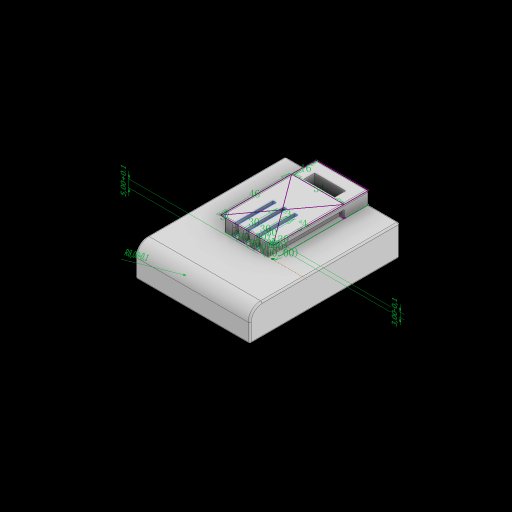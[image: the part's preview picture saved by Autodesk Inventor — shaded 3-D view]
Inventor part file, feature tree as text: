
AUTODESK INVENTOR PART (.ipt)
format: ipt  version: 2023 (Build 270158030, 158C)  size: 745,472 bytes
history: native  units: mm
features: extrude x9, sketch x7, fillet x7, other x3, chamfer x2
ambient origin geometry x8: Origin, YZ Plane, XZ Plane, XY Plane, X Axis, Y Axis, Z Axis, Center Point
bodies: 实体1 (feature_tree)
feature tree (28):
  extrude  "拉伸1"  Depth=46.0mm
  sketch  "草图2"  dims[d8=16.0mm d9=3.0mm]
  extrude  "拉伸2"  Depth=16.0mm
  extrude  "拉伸3"  Depth=5.0mm
  sketch  "草图4"  dims[d10=5.0mm d11=3.0mm]
  extrude  "拉伸4"  Depth=8.0mm TaperAngle=0.0deg
  extrude  "拉伸5"  Depth=3.0mm TaperAngle=0.0deg
  extrude  "拉伸6"  TaperAngle=90.0deg  [1 undecoded]
  fillet  "圆角1"  Radius=3.0mm
  extrude  "拉伸8"  TaperAngle=90.0deg  [1 undecoded]
  fillet  "圆角2"  Radius=4.0mm
  extrude  "拉伸9"  Depth=8.0mm
  extrude  "拉伸10"  TaperAngle=90.0deg  [1 undecoded]
  fillet  "圆角3"  Radius=30.0mm
  fillet  "圆角4"  [1 undecoded]
  fillet  "圆角5"  Radius=8.0mm
  fillet  "圆角6"  Radius=5.0mm
  chamfer  "倒角1"  Distance=20.0mm
  chamfer  "倒角2"  [1 undecoded]
  fillet  "圆角7"  Radius=35.0mm
  sketch  "草图1"  dims[d0=34.0mm d1=46.0mm]
  sketch  "草图5"  dims[d12=5.0mm d13=8.0mm d14=0.0mm]
  sketch  "草图7"  dims[d15=3.0mm d16=0.0mm d17=3.0mm d18=0.0mm]
  sketch  "草图8"  dims[d21=30.0mm d22=90.0deg d24=3.0mm]
  sketch  "草图9"  dims[d27=30.0mm d28=90.0deg d29=4.0mm d30=30.0mm d31=90.0deg d32=30.0mm d33=90.0deg d34=8.0mm d35=0.0mm d36=5.0mm d37=0.0mm d38=20.0mm d39=0.0mm d40=35.0mm d41=20.0mm d42=35.0mm d43=10.0mm d44=0.0mm d45=8.0mm d57=5.0mm d58=5.0mm d59=5.0mm d60=5.0mm d61=0.0mm d62=5.0mm d63=5.0mm d64=92.0mm d65=90.0deg d66=64.0mm d67=10.0mm d68=0.0mm d69=5.0mm d70=5.0mm d71=5.0mm d72=4.0mm d73=0.0mm d74=1.0mm d75=1.0mm d76=1.0mm d77=1.0mm d78=10.0mm d79=2.0mm d80=45.0deg d81=5.0mm d82=2.0mm d83=60.0deg d84=5.0mm d90=2.342509mm d91=8.298847mm d92=5.0mm d93=3.0mm d94=36.708657mm d95=5.765193mm d96=2.781092mm d97=8.0mm]
  other  "线性尺寸 1"
  other  "线性尺寸 2"
  other  "半径尺寸 1"
note: 5 required parameter values undecoded (feature->parameter linkage not recoverable at this tier; creation-order binding heuristic only, values carry confidence <= 0.55)
